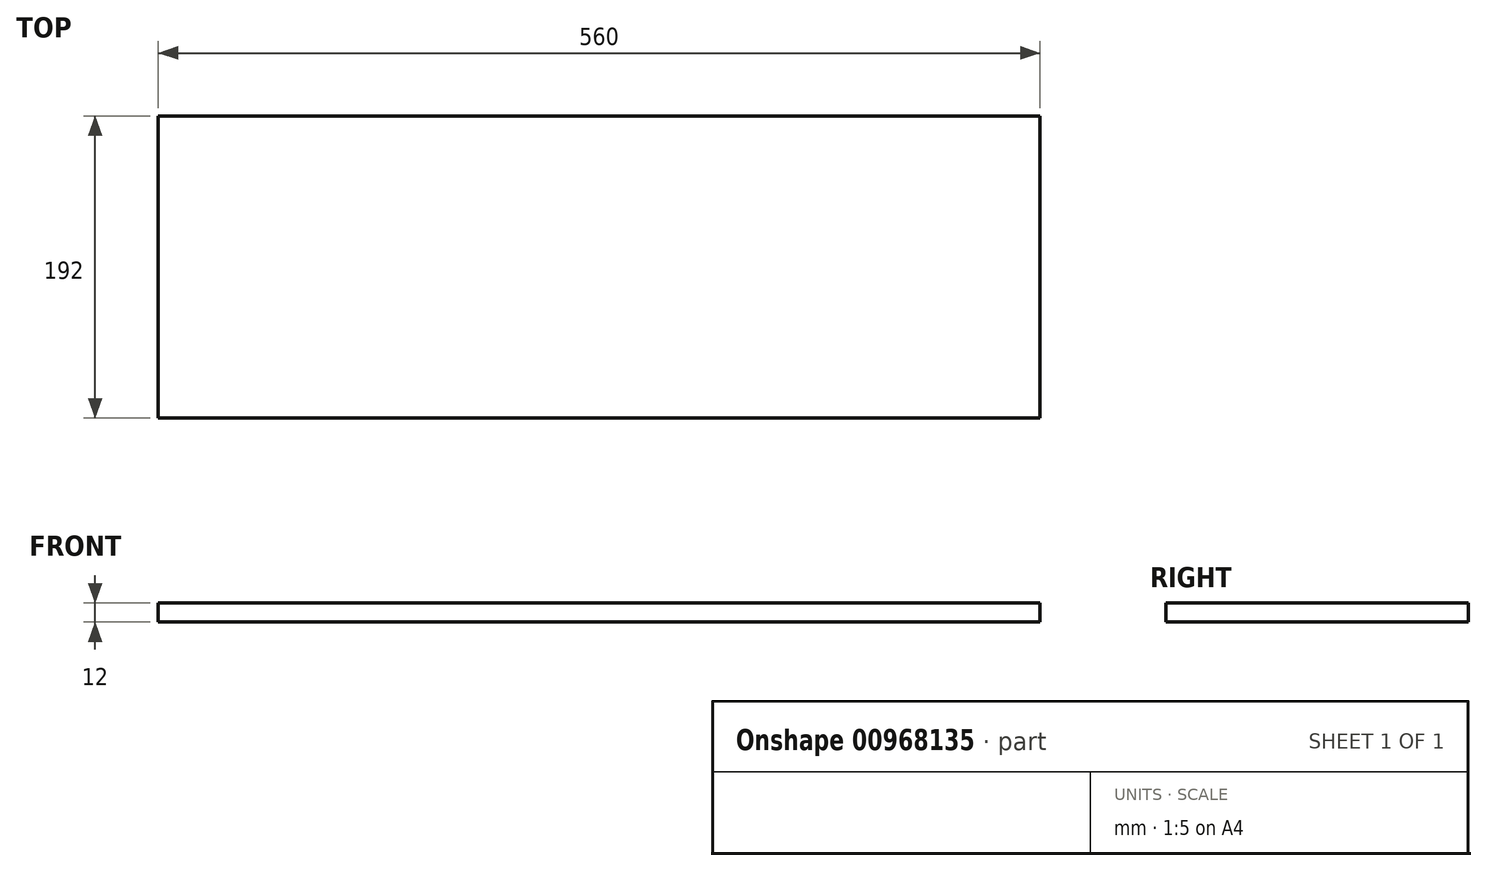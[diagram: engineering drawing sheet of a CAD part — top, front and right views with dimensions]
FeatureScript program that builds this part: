
annotation { "Feature Type Name" : "Feature", "Feature Type Description" : "" }
export const myFeature = defineFeature(function(context is Context, id is Id, definition is map)
    precondition{}
    {
        {
            var Q0;
            Q0=qCreatedBy(makeId("Top.planeOp"),FACE);
            var sketch = newSketch(context, id + "F0", { "sketchPlane" : qUnion([Q0])});
            skLineSegment(sketch, "E0.bottom", {"start": v(-281.72, -119.03) * mm, "end": v(278.28, -119.03) * mm});
            skLineSegment(sketch, "E0.top", {"start": v(-281.72, 72.97) * mm, "end": v(278.28, 72.97) * mm});
            skLineSegment(sketch, "E0.left", {"start": v(-281.72, -119.03) * mm, "end": v(-281.72, 72.97) * mm});
            skLineSegment(sketch, "E0.right", {"start": v(278.28, -119.03) * mm, "end": v(278.28, 72.97) * mm});
            skSolve(sketch);
        }
        {
            var Q0;
            Q0 = qSketchRegion(id + "F0", true);
            extrude(context, id + "F1", {"entities" : qUnion([Q0]), "depth" : 12 * mm, "offsetDistance" : 25 * mm});
        }
    });
